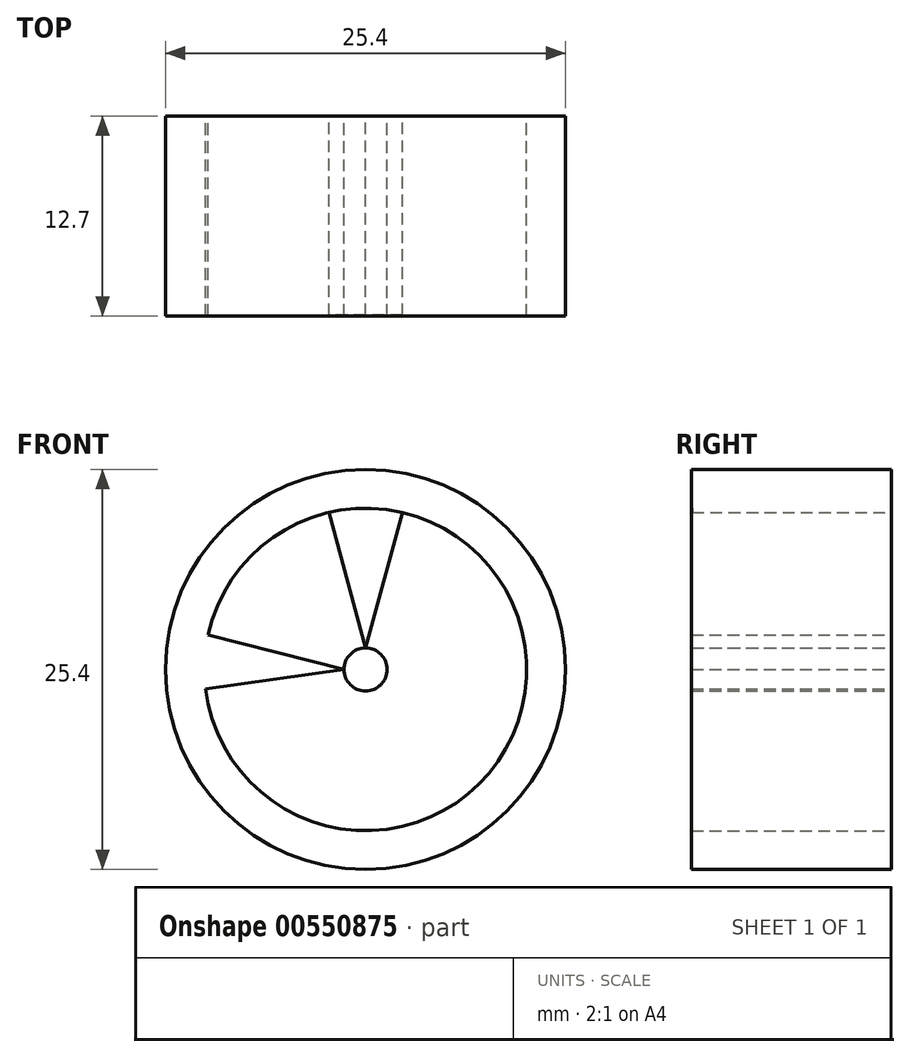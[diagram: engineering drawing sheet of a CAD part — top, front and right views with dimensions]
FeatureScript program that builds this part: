
annotation { "Feature Type Name" : "Feature", "Feature Type Description" : "" }
export const myFeature = defineFeature(function(context is Context, id is Id, definition is map)
    precondition{}
    {
        {
            var Q0;
            Q0=qCreatedBy(makeId("Front.planeOp"),FACE);
            var sketch = newSketch(context, id + "F0", { "sketchPlane" : qUnion([Q0])});
            skCircle(sketch, "E0", {"center": v(0, 0) * mm, "radius": 12.7 * mm});
            skCircle(sketch, "E1", {"center": v(0, 0) * mm, "radius": 10.24 * mm});
            skCircle(sketch, "E2", {"center": v(0, 0) * mm, "radius": 1.37 * mm});
            skLineSegment(sketch, "E3", {"start": v(0, -1.37) * mm, "end": v(0, -10.24) * mm});
            skLineSegment(sketch, "E4", {"start": v(1.37, 0) * mm, "end": v(10.24, 0) * mm});
            skLineSegment(sketch, "E5", {"start": v(-1.37, 0) * mm, "end": v(-10, 2.18) * mm});
            skLineSegment(sketch, "E6", {"start": v(-1.37, 0) * mm, "end": v(-10.16, -1.23) * mm});
            skLineSegment(sketch, "E7", {"start": v(0, 1.37) * mm, "end": v(-2.32, 9.97) * mm});
            skLineSegment(sketch, "E8", {"start": v(0, 1.37) * mm, "end": v(2.34, 9.97) * mm});
            skSolve(sketch);
        }
        {
            var Q0;
            Q0=makeQuery(id+"F0.imprint","IMPRINT",FACE,{"disambiguationData":[TD([[makeQuery(id+"F0.imprint","IMPRINT",EDGE,{"derivedFrom":sQuery(id+"F0.wireOp",EDGE,"E0")}),1.0]])]});
            extrude(context, id + "F1", {"entities" : qUnion([Q0]), "depth" : 12.7 * mm, "offsetDistance" : 25.4 * mm});
        }
        {
            var Q0;
            {var subQ0=sQuery(id+"F0.wireOp",EDGE,"E5");Q0=makeQuery(id+"F0.imprint","IMPRINT",FACE,{"disambiguationData":[TD([[makeQuery(id+"F0.imprint","IMPRINT",EDGE,{"derivedFrom":subQ0}),1.0]])]});}
            extrude(context, id + "F2", {"entities" : qUnion([Q0]), "operationType" : NewBodyOperationType.ADD, "depth" : 12.7 * mm, "offsetDistance" : 25.4 * mm});
        }
        {
            var Q0;
            {var subQ0=sQuery(id+"F0.wireOp",EDGE,"E2");var subQ1=makeQuery(id+"F0.imprint","INTERSECT",VERTEX,{"derivedFrom":[subQ0,sQuery(id+"F0.wireOp",EDGE,"Jukm25ur-4RfZ-Ijsa-qAIY-OH1upS2KYeSY")]});Q0=makeQuery(id+"F0.imprint","IMPRINT",FACE,{"disambiguationData":[TD([[makeQuery(id+"F0.imprint","IMPRINT",EDGE,{"disambiguationData":[TD([[subQ1,1.0]])],"derivedFrom":subQ0}),1.0]])]});}
            extrude(context, id + "F3", {"entities" : qUnion([Q0]), "depth" : 12.7 * mm, "offsetDistance" : 25.4 * mm});
        }
        {
            var Q0;
            {var subQ0=sQuery(id+"F0.wireOp",EDGE,"E7");Q0=makeQuery(id+"F0.imprint","IMPRINT",FACE,{"disambiguationData":[TD([[makeQuery(id+"F0.imprint","IMPRINT",EDGE,{"derivedFrom":subQ0}),-1.0]])]});}
            extrude(context, id + "F4", {"entities" : qUnion([Q0]), "operationType" : NewBodyOperationType.ADD, "depth" : 12.65 * mm, "offsetDistance" : 25.4 * mm});
        }
    });
